# Revit family: Maxlogic Diğer Sistem SGC Modülü
name_source: partatom
category: Fire Alarm Devices
units: mm (PartAtom-declared; Revit-internal decimal feet)

## family parameters
Cut with Voids When Loaded = No
Host = Face
Maintain Annotation Orientation = Yes
OmniClass Number = 23.85.30.21
OmniClass Title = Environmental Detection/Registration
Part Type = Normal
Room Calculation Point = No
Round Connector Dimension = Use Diameter
Shared = No

## types (2) — shared parameters
Code Performance = EN 54-18
Color = Beyaz
External supply = 24 V DC
Fax Number = (+)90 216 466 45 10
Installation Manual = https://mavilielektronik.com
Main Material = White Plastic PC/ABS
Manufacturer = Mavili Elektronik Ticaret A.Ş.
Model = MaxLogic
Mounting surface = Duvara montaj
Nominal Depth = 52 mm
Nominal Height = 100 mm
Nominal Width = 100 mm
Operating temperature = (-10°C) - (+55°C)
Operating voltage range = 18-33V/DC
Operatonal Voltage (default) = 26 V/DC
Secondary Material = Plastic
URL = https://www.mavili.com.tr
Warranty Duration Labor = 2
Warranty Duration Parts = 2
Warranty Duration Unit = Year
Weight = 155 gr
zero-valued in all types: Cost, Default Elevation

## per-type parameters (varying)
| type | Description | Product Code |
| Maxlogic Diğer Sistem SGC Modülü, TCP/IP Çıkışlı | Diğer Sistem SGC Modülü, TCP/IP Çıkışlı | ML-12012.C |
| Diğer Sistemler ile Supervisor Arası Haberleşme SGC Kartı UART Çıkışlı (kablo dahil) | Diğer Sistemler ile Supervisor Arası Haberleşme SGC Kartı UART Çıkışlı (kablo dahil) | ML-12012.UART |

## geometry (parser evidence)
native form markers: Sweep x2
no freeform markers — native parametric forms only
